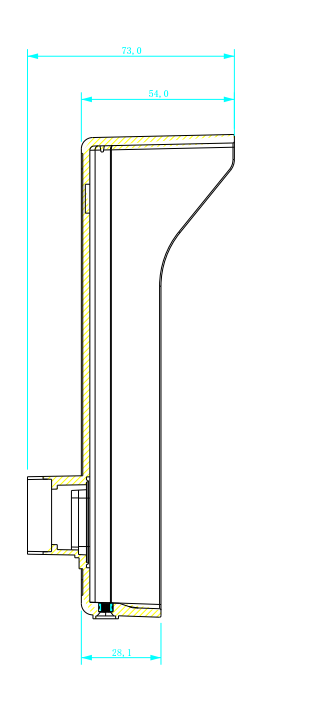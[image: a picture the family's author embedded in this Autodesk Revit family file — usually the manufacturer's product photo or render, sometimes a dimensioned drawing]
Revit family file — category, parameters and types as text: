
# Revit family: AT-07
name_source: partatom
category: Устройства связи
units: mm (PartAtom-declared; Revit-internal decimal feet)

## family parameters
Всегда вертикально = Нет
На основе рабочей плоскости = Да
Общий = Да
При загрузке вырезать с полостями = Нет
Размер круглого соединителя = Использовать диаметр
Сохранять ориентацию аннотаций = Нет
Тип детали = Нормальный
Точка принадлежности помещению = Нет

## types (1)
- AT-07
    ADSK_URL документации изделия = http://cdn.bas-ip.com
    ADSK_URL страницы изделия = https://www.bas-ip.ru
    ADSK_Версия Revit = Revit 2020
    ADSK_Единица измерения = шт
    ADSK_Завод-изготовитель = BAS-IP
    ADSK_Классификация нагрузок = Внутренний монитор индивидуальный
    ADSK_Количество фаз = 1
    ADSK_Коэффициент мощности = 0.9
    ADSK_Марка = AT-07
    ADSK_Наименование = Внутренний монитор индивидуальный AT-07
    ADSK_Наименование краткое = AT-07
    ADSK_Напряжение = 12 В
    ADSK_Номинальная мощность = 6 Вт
    ADSK_Полная мощность = 6 В·А
    ADSK_Размер_Длина = 128 мм
    ADSK_Размер_Толщина = 27 мм
    ADSK_Размер_Ширина = 236 мм
    BIM library = https://bimlib.ru
    URL = https://www.bas-ip.ru
    Автоответчик = Есть
    Бекап фото сделанных во время вызова = Есть, на SD карту
    Возможность установки сторонних приложений = Есть
    Встроенная камера = Нет
    Выбор типа заставки в режиме ожидания = Квадратор 
Часы 
Фоторамка 
Тур по времени 
IP камера (постоянный просмотр)
    Группа модели = Внутренний монитор индивидуальный AT-07
    Дисплей = 7” IPS LCD, сенсорный емкостный
    Дополнительные разъемы = Слот для microSD карт (SDHC)
    Загрузка пользовательских MP3 мелодий = Есть
    Изготовитель = BAS-IP
    Изображение типоразмера = <Нет>
    Интерфейс = Многоязычный графический
    Количество IP камер = До 32 камер
    Количество индивидуальных вызывных панелей = До 9 панелей
    Количество мелодий вызова = 9 мелодий на выбор
    Количество многоабонентских вызывных панелей = До 9 панелей
    Корпус = Алюминий
    Материал корпуса = Материал серый
    Мультимедиа возможности = Просмотр видео-, фото- и аудиофайлов с SD карты
    Обновление программного обеспечения = Через WEB-интерфейс, из SD карты, из сервера обновлений BAS-IP
    Описание = Внутренний монитор индивидуальный AT-07 - Внутренний видеодомофон работает под управлением операционной системы Android 6.0. Он поставляется в 4 цветовых вариациях: white, gold, black, silver и имеет два варианта установки: настенное накладное крепление и крепление врезным монтажом с использованием специального кронштейна
    Отметка по умолчанию = 0 мм
    Питание = PoE  и +12 Вольт
    Поддержка получения сообщений = Есть
    Поддержка сторонних виджетов = Есть
    Подключение дополнительных мониторов = До 8 мониторов
    Потребление питания = 6 Вт, в режиме ожидания – 2,5 Вт
    Размеры = 236 x 128 x 26,5 мм
    Размеры дисплея = 155,0×86,0 мм
    Разрешение экрана = 1024×600
    Режим "Без звука" = Есть, настраиваемый по времени
    Режим "Не беспокоить" = Есть, настраиваемый по времени
    Режим "Ожидания" = Есть, настраиваемый по времени
    Сценарии = Есть
    Тип интеркома = Аудиоинтерком
    Тип установки = Настенная накладная, врезная с помощью кронштейна
    Управление домашней автоматикой = Свет, шторы, лифт
    Функция памяти = Запись фото, видео и аудио на SD карту
    Цветовое решение = Black, White, Silver, Gold
